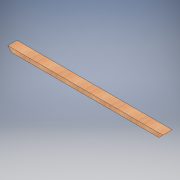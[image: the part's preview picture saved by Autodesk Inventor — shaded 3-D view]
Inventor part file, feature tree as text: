
AUTODESK INVENTOR PART (.ipt)
format: ipt  version: 2016 (Build 200138000, 138)  size: 99,328 bytes
history: native  units: in
note: dims shown in document units (in); Inventor stores cm internally (conversion verified against a paired STEP export)
features: extrude x1, sketch x1
ambient origin geometry x8: Origin, YZ Plane, XZ Plane, XY Plane, X Axis, Y Axis, Z Axis, Center Point
bodies: Body1 (feature_tree)
feature tree (2):
  extrude  "Extrusion2"  TaperAngle=135.0deg  [1 undecoded]
  sketch  "Sketch2"  dims[d10=45.0deg d11=135.0deg d12=3.5in d13=0.0in d14=58.0in d15=1.5in]
note: 1 required parameter value undecoded (feature->parameter linkage not recoverable at this tier; creation-order binding heuristic only, values carry confidence <= 0.55)
